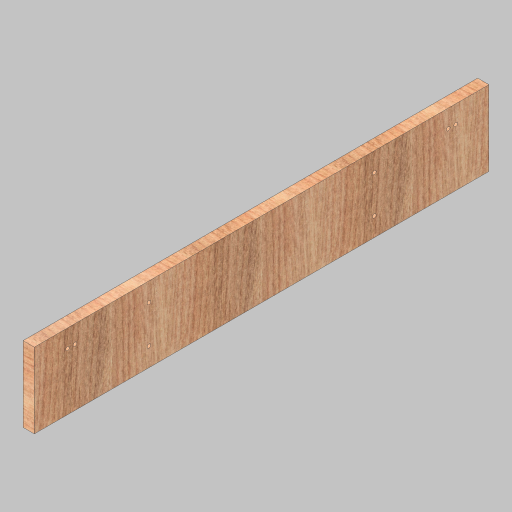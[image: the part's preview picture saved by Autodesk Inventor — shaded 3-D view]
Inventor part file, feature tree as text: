
AUTODESK INVENTOR PART (.ipt)
format: ipt  version: 2023.5 (Build 275446000, 446)  size: 230,912 bytes
history: native  units: in
note: dims shown in document units (in); Inventor stores cm internally (conversion verified against a paired STEP export)
features: sketch x2, extrude x1, hole x1
ambient origin geometry x8: Origin, YZ Plane, XZ Plane, XY Plane, X Axis, Y Axis, Z Axis, Center Point
bodies: Solid1 (feature_tree)
feature tree (4):
  extrude  "Extrusion1"  Depth=30.25in
  hole  "Hole1"  [1 undecoded]
  sketch  "Sketch1"  dims[d0=5.0in d1=30.25in]
  sketch  "Sketch2"  dims[d2=0.75in d3=0.0in d4=0.5in d5=2.211in d6=1.188in d7=0.25in d8=0.75in d9=0.375in d10=0.25in d11=0.5635in d12=1.0in d13=0.8108in d14=2.5in d15=7.5in]
note: 1 required parameter value undecoded (feature->parameter linkage not recoverable at this tier; creation-order binding heuristic only, values carry confidence <= 0.55)
